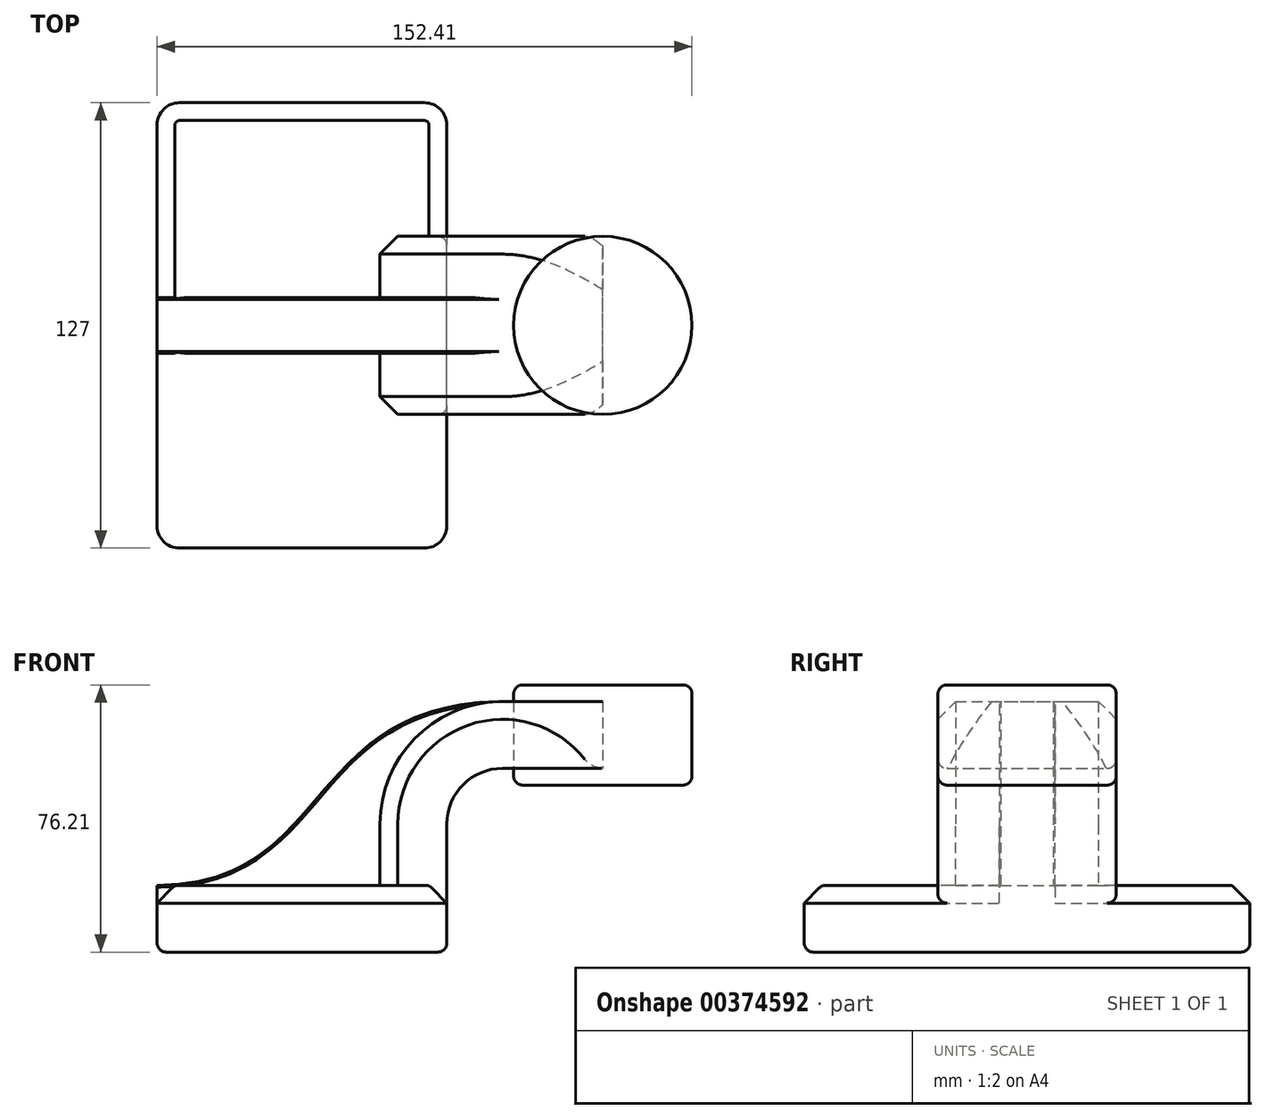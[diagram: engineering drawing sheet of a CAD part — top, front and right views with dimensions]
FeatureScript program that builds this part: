
annotation { "Feature Type Name" : "Feature", "Feature Type Description" : "" }
export const myFeature = defineFeature(function(context is Context, id is Id, definition is map)
    precondition{}
    {
        {
            var Q0;
            Q0=qCreatedBy(makeId("Front.planeOp"),FACE);
            var sketch = newSketch(context, id + "F0", { "sketchPlane" : qUnion([Q0])});
            skLineSegment(sketch, "E0.bottom", {"start": v(-41.28, 9.52) * mm, "end": v(41.27, 9.53) * mm});
            skLineSegment(sketch, "E0.top", {"start": v(-41.28, -9.53) * mm, "end": v(41.28, -9.53) * mm});
            skLineSegment(sketch, "E0.left", {"start": v(-41.28, 9.52) * mm, "end": v(-41.27, -9.53) * mm});
            skLineSegment(sketch, "E0.right", {"start": v(41.28, 9.53) * mm, "end": v(41.28, -9.52) * mm});
            skPoint(sketch, "E0.middle", {"position": v(0, 0) * mm});
            skLineSegment(sketch, "E1.bottom", {"start": v(60.32, 66.68) * mm, "end": v(111.12, 66.68) * mm});
            skLineSegment(sketch, "E1.top", {"start": v(60.32, 38.1) * mm, "end": v(111.12, 38.1) * mm});
            skLineSegment(sketch, "E1.left", {"start": v(60.32, 66.68) * mm, "end": v(60.32, 38.1) * mm});
            skLineSegment(sketch, "E1.right", {"start": v(111.12, 66.68) * mm, "end": v(111.12, 38.1) * mm});
            skPoint(sketch, "E1.middle", {"position": v(85.72, 52.39) * mm});
            skLineSegment(sketch, "E2", {"start": v(41.27, 9.53) * mm, "end": v(41.27, 27) * mm});
            skArc(sketch, "E3", {"start": v(41.27, 27) * mm, "mid": v(45.92, 38.23) * mm, "end": v(57.15, 42.88) * mm});
            skLineSegment(sketch, "E4", {"start": v(57.15, 42.88) * mm, "end": v(85.72, 42.88) * mm});
            skPoint(sketch, "E4.endSnap0", {"position": v(85.72, 38.1) * mm});
            skLineSegment(sketch, "E5.0", {"start": v(57.15, 61.93) * mm, "end": v(85.72, 61.93) * mm});
            skArc(sketch, "E5.1", {"start": v(22.22, 27) * mm, "mid": v(32.45, 51.7) * mm, "end": v(57.15, 61.93) * mm});
            skLineSegment(sketch, "E5.2", {"start": v(22.22, 9.53) * mm, "end": v(22.22, 27) * mm});
            skLineSegment(sketch, "E6", {"start": v(85.72, 38.1) * mm, "end": v(85.72, 66.68) * mm});
            skFitSpline(sketch, "E7", {"points": [v(-41.28, 9.52) * mm, v(57.15, 61.93) * mm], "startDerivative": vector(150.82, 0) * mm, "endDerivative": vector(171.45, 1.6) * mm});
            skSolve(sketch);
        }
        {
            var Q0;
            Q0=makeQuery(id+"F0.imprint","IMPRINT",FACE,{"disambiguationData":[TD([[makeQuery(id+"F0.imprint","IMPRINT",EDGE,{"derivedFrom":sQuery(id+"F0.wireOp",EDGE,"E0.top")}),1.0]])]});
            extrude(context, id + "F1", {"entities" : qUnion([Q0]), "endBound" : BoundingType.SYMMETRIC, "depth" : 127 * mm});
        }
        {
            var Q0;
            {var subQ1=sQuery(id+"F0.wireOp",EDGE,"E2");Q0=makeQuery(id+"F0.imprint","IMPRINT",FACE,{"disambiguationData":[TD([[makeQuery(id+"F0.imprint","IMPRINT",EDGE,{"derivedFrom":subQ1}),1.0]])]});}
            var Q1;
            {var subQ0=sQuery(id+"F0.wireOp",EDGE,"E5.0");var subQ1=sQuery(id+"F0.wireOp",EDGE,"E1.left");var subQ2=makeQuery(id+"F0.imprint","INTERSECT",VERTEX,{"derivedFrom":[subQ1,subQ0]});Q1=makeQuery(id+"F0.imprint","IMPRINT",FACE,{"disambiguationData":[TD([[makeQuery(id+"F0.imprint","IMPRINT",EDGE,{"disambiguationData":[TD([[subQ2,-1.0]])],"derivedFrom":subQ1}),1.0]])]});}
            extrude(context, id + "F2", {"entities" : qUnion([Q0, Q1]), "operationType" : NewBodyOperationType.ADD, "endBound" : BoundingType.SYMMETRIC, "depth" : 50.8 * mm});
        }
        {
            var Q0;
            {var subQ3=sQuery(id+"F0.wireOp",EDGE,"E5.2");Q0=makeQuery(id+"F0.imprint","IMPRINT",FACE,{"disambiguationData":[TD([[makeQuery(id+"F0.imprint","IMPRINT",EDGE,{"derivedFrom":subQ3}),1.0]])]});}
            extrude(context, id + "F3", {"entities" : qUnion([Q0]), "operationType" : NewBodyOperationType.ADD, "endBound" : BoundingType.SYMMETRIC, "depth" : 15.88 * mm});
        }
        {
            var Q0;
            {var subQ4=sQuery(id+"F0.wireOp",EDGE,"E1.right");Q0=makeQuery(id+"F0.imprint","IMPRINT",FACE,{"disambiguationData":[TD([[makeQuery(id+"F0.imprint","IMPRINT",EDGE,{"derivedFrom":subQ4}),-1.0]])]});}
            var Q1;
            Q1=sQuery(id+"F0.wireOp",EDGE,"E6");
            revolve(context, id + "F4", {"entities" : qUnion([Q0]), "axis" : qUnion([Q1]), "revolveType" : RevolveType.FULL});
        }
        {
            var Q0;
            Q0=makeQuery(id+"F1.opExtrude","CAP_EDGE",EDGE,{"disambiguationData":[OSD([sQuery(id+"F0.wireOp",EDGE,"E0.left")])],"isStart":false});
            var Q1;
            Q1=makeQuery(id+"F1.opExtrude","CAP_EDGE",EDGE,{"disambiguationData":[OSD([sQuery(id+"F0.wireOp",EDGE,"E0.right")])],"isStart":false});
            var Q2;
            Q2=makeQuery(id+"F1.opExtrude","CAP_EDGE",EDGE,{"disambiguationData":[OSD([sQuery(id+"F0.wireOp",EDGE,"E0.right")])],"isStart":true});
            var Q3;
            Q3=makeQuery(id+"F1.opExtrude","CAP_EDGE",EDGE,{"disambiguationData":[OSD([sQuery(id+"F0.wireOp",EDGE,"E0.left")])],"isStart":true});
            fillet(context, id + "F5", {"entities" : qUnion([Q0, Q1, Q2, Q3]), "radius" : 6.35 * mm, "tangentPropagation" : true, "allowEdgeOverflow" : false});
        }
        {
            var Q0;
            Q0=makeQuery(id+"F1.opExtrude","CAP_EDGE",EDGE,{"disambiguationData":[OSD([sQuery(id+"F0.wireOp",EDGE,"E0.bottom")])],"isStart":false});
            var Q1;
            {var subQ4=sQuery(id+"F0.wireOp",EDGE,"E0.bottom");var subQ5=sQuery(id+"F0.wireOp",EDGE,"E0.right");var subQ6=sQuery(id+"F0.wireOp",EDGE,"E0.left");Q1=makeQuery(id+"F5.opFillet","BLEND_EDGE",EDGE,{"blendedFrom":[makeQuery(id+"F1.opExtrude","CAP_EDGE",EDGE,{"disambiguationData":[OSD([subQ6])],"isStart":false}),makeQuery(id+"F3.boolean.opBoolean","SPLIT",FACE,{"disambiguationData":[TD([makeQuery(id+"F1.opExtrude","CAP_FACE",FACE,{"disambiguationData":[OSD([subQ4,sQuery(id+"F0.wireOp",EDGE,"E0.top"),subQ6,subQ5])],"isStart":false})])],"derivedFrom":makeQuery(id+"F1.opExtrude","SWEPT_FACE",FACE,{"disambiguationData":[OSD([subQ4])]})})],"blendedInto":[makeQuery(id+"F3.boolean.opBoolean","SPLIT",FACE,{"disambiguationData":[TD([makeQuery(id+"F1.opExtrude","CAP_FACE",FACE,{"disambiguationData":[OSD([subQ4,sQuery(id+"F0.wireOp",EDGE,"E0.top"),subQ6,subQ5])],"isStart":false})])],"derivedFrom":makeQuery(id+"F1.opExtrude","SWEPT_FACE",FACE,{"disambiguationData":[OSD([subQ4])]})})]});}
            var Q2;
            {var subQ4=sQuery(id+"F0.wireOp",EDGE,"E0.bottom");var subQ5=sQuery(id+"F0.wireOp",EDGE,"E0.right");var subQ6=sQuery(id+"F0.wireOp",EDGE,"E0.left");Q2=makeQuery(id+"F5.opFillet","BLEND_EDGE",EDGE,{"blendedFrom":[makeQuery(id+"F1.opExtrude","CAP_EDGE",EDGE,{"disambiguationData":[OSD([subQ5])],"isStart":false}),makeQuery(id+"F3.boolean.opBoolean","SPLIT",FACE,{"disambiguationData":[TD([makeQuery(id+"F1.opExtrude","CAP_FACE",FACE,{"disambiguationData":[OSD([subQ4,sQuery(id+"F0.wireOp",EDGE,"E0.top"),subQ6,subQ5])],"isStart":false})])],"derivedFrom":makeQuery(id+"F1.opExtrude","SWEPT_FACE",FACE,{"disambiguationData":[OSD([subQ4])]})})],"blendedInto":[makeQuery(id+"F3.boolean.opBoolean","SPLIT",FACE,{"disambiguationData":[TD([makeQuery(id+"F1.opExtrude","CAP_FACE",FACE,{"disambiguationData":[OSD([subQ4,sQuery(id+"F0.wireOp",EDGE,"E0.top"),subQ6,subQ5])],"isStart":false})])],"derivedFrom":makeQuery(id+"F1.opExtrude","SWEPT_FACE",FACE,{"disambiguationData":[OSD([subQ4])]})})]});}
            var Q3;
            {var subQ0=sQuery(id+"F0.wireOp",EDGE,"E2");var subQ1=sQuery(id+"F0.wireOp",EDGE,"E0.bottom");var subQ2=sQuery(id+"F0.wireOp",EDGE,"E0.right");Q3=makeQuery(id+"F2.boolean.opBoolean","SPLIT",EDGE,{"disambiguationData":[TD([makeQuery(id+"F1.opExtrude","CAP_FACE",FACE,{"disambiguationData":[OSD([subQ1,sQuery(id+"F0.wireOp",EDGE,"E0.top"),sQuery(id+"F0.wireOp",EDGE,"E0.left"),subQ2])],"isStart":false})])],"derivedFrom":makeQuery(id+"F1.opExtrude","SWEPT_EDGE",EDGE,{"disambiguationData":[OSD([subQ1,subQ2,subQ0])]})});}
            var Q4;
            {var subQ0=sQuery(id+"F0.wireOp",EDGE,"E7");var subQ1=sQuery(id+"F0.wireOp",EDGE,"E0.bottom");var subQ2=sQuery(id+"F0.wireOp",EDGE,"E0.left");Q4=makeQuery(id+"F3.boolean.opBoolean","SPLIT",EDGE,{"disambiguationData":[TD([makeQuery(id+"F1.opExtrude","CAP_FACE",FACE,{"disambiguationData":[OSD([subQ1,sQuery(id+"F0.wireOp",EDGE,"E0.top"),subQ2,sQuery(id+"F0.wireOp",EDGE,"E0.right")])],"isStart":false})])],"derivedFrom":makeQuery(id+"F1.opExtrude","SWEPT_EDGE",EDGE,{"disambiguationData":[OSD([subQ1,subQ2,subQ0])]})});}
            var Q5;
            {var subQ0=sQuery(id+"F0.wireOp",EDGE,"E0.left");var subQ1=sQuery(id+"F0.wireOp",EDGE,"E7");var subQ2=sQuery(id+"F0.wireOp",EDGE,"E0.bottom");Q5=makeQuery(id+"F3.boolean.opBoolean","SPLIT",EDGE,{"disambiguationData":[TD([makeQuery(id+"F1.opExtrude","CAP_FACE",FACE,{"disambiguationData":[OSD([subQ2,sQuery(id+"F0.wireOp",EDGE,"E0.top"),subQ0,sQuery(id+"F0.wireOp",EDGE,"E0.right")])],"isStart":true})])],"derivedFrom":makeQuery(id+"F1.opExtrude","SWEPT_EDGE",EDGE,{"disambiguationData":[OSD([subQ2,subQ0,subQ1])]})});}
            var Q6;
            {var subQ4=sQuery(id+"F0.wireOp",EDGE,"E0.bottom");var subQ5=sQuery(id+"F0.wireOp",EDGE,"E0.right");var subQ6=sQuery(id+"F0.wireOp",EDGE,"E0.left");Q6=makeQuery(id+"F5.opFillet","BLEND_EDGE",EDGE,{"blendedFrom":[makeQuery(id+"F1.opExtrude","CAP_EDGE",EDGE,{"disambiguationData":[OSD([subQ6])],"isStart":true}),makeQuery(id+"F3.boolean.opBoolean","SPLIT",FACE,{"disambiguationData":[TD([makeQuery(id+"F1.opExtrude","CAP_FACE",FACE,{"disambiguationData":[OSD([subQ4,sQuery(id+"F0.wireOp",EDGE,"E0.top"),subQ6,subQ5])],"isStart":true})])],"derivedFrom":makeQuery(id+"F1.opExtrude","SWEPT_FACE",FACE,{"disambiguationData":[OSD([subQ4])]})})],"blendedInto":[makeQuery(id+"F3.boolean.opBoolean","SPLIT",FACE,{"disambiguationData":[TD([makeQuery(id+"F1.opExtrude","CAP_FACE",FACE,{"disambiguationData":[OSD([subQ4,sQuery(id+"F0.wireOp",EDGE,"E0.top"),subQ6,subQ5])],"isStart":true})])],"derivedFrom":makeQuery(id+"F1.opExtrude","SWEPT_FACE",FACE,{"disambiguationData":[OSD([subQ4])]})})]});}
            var Q7;
            Q7=makeQuery(id+"F1.opExtrude","CAP_EDGE",EDGE,{"disambiguationData":[OSD([sQuery(id+"F0.wireOp",EDGE,"E0.bottom")])],"isStart":true});
            var Q8;
            {var subQ4=sQuery(id+"F0.wireOp",EDGE,"E0.bottom");var subQ5=sQuery(id+"F0.wireOp",EDGE,"E0.right");var subQ6=sQuery(id+"F0.wireOp",EDGE,"E0.left");Q8=makeQuery(id+"F5.opFillet","BLEND_EDGE",EDGE,{"blendedFrom":[makeQuery(id+"F1.opExtrude","CAP_EDGE",EDGE,{"disambiguationData":[OSD([subQ5])],"isStart":true}),makeQuery(id+"F3.boolean.opBoolean","SPLIT",FACE,{"disambiguationData":[TD([makeQuery(id+"F1.opExtrude","CAP_FACE",FACE,{"disambiguationData":[OSD([subQ4,sQuery(id+"F0.wireOp",EDGE,"E0.top"),subQ6,subQ5])],"isStart":true})])],"derivedFrom":makeQuery(id+"F1.opExtrude","SWEPT_FACE",FACE,{"disambiguationData":[OSD([subQ4])]})})],"blendedInto":[makeQuery(id+"F3.boolean.opBoolean","SPLIT",FACE,{"disambiguationData":[TD([makeQuery(id+"F1.opExtrude","CAP_FACE",FACE,{"disambiguationData":[OSD([subQ4,sQuery(id+"F0.wireOp",EDGE,"E0.top"),subQ6,subQ5])],"isStart":true})])],"derivedFrom":makeQuery(id+"F1.opExtrude","SWEPT_FACE",FACE,{"disambiguationData":[OSD([subQ4])]})})]});}
            var Q9;
            {var subQ0=sQuery(id+"F0.wireOp",EDGE,"E2");var subQ1=sQuery(id+"F0.wireOp",EDGE,"E0.bottom");var subQ2=sQuery(id+"F0.wireOp",EDGE,"E0.right");Q9=makeQuery(id+"F2.boolean.opBoolean","SPLIT",EDGE,{"disambiguationData":[TD([makeQuery(id+"F1.opExtrude","CAP_FACE",FACE,{"disambiguationData":[OSD([subQ1,sQuery(id+"F0.wireOp",EDGE,"E0.top"),sQuery(id+"F0.wireOp",EDGE,"E0.left"),subQ2])],"isStart":true})])],"derivedFrom":makeQuery(id+"F1.opExtrude","SWEPT_EDGE",EDGE,{"disambiguationData":[OSD([subQ1,subQ2,subQ0])]})});}
            var Q10;
            Q10=makeQuery(id+"F2.opExtrude","CAP_EDGE",EDGE,{"disambiguationData":[OSD([sQuery(id+"F0.wireOp",EDGE,"E5.2")])],"isStart":false});
            var Q11;
            Q11=makeQuery(id+"F2.opExtrude","CAP_EDGE",EDGE,{"disambiguationData":[OSD([sQuery(id+"F0.wireOp",EDGE,"E5.1")])],"isStart":true});
            chamfer(context, id + "F6", {"entities" : qUnion([Q0, Q1, Q2, Q3, Q4, Q5, Q6, Q7, Q8, Q9, Q10, Q11]), "width" : 5.08 * mm, "tangentPropagation" : true});
        }
        {
            var Q0;
            Q0=makeQuery(id+"F3.opExtrude","CAP_EDGE",EDGE,{"disambiguationData":[OSD([sQuery(id+"F0.wireOp",EDGE,"E7")])],"isStart":false});
            var Q1;
            Q1=makeQuery(id+"F3.opExtrude","CAP_EDGE",EDGE,{"disambiguationData":[OSD([sQuery(id+"F0.wireOp",EDGE,"E7")])],"isStart":true});
            chamfer(context, id + "F7", {"entities" : qUnion([Q0, Q1]), "width" : 0.5 * mm, "tangentPropagation" : true});
        }
        {
            var Q0;
            Q0=makeQuery(id+"F4.opRevolve","SWEPT_EDGE",EDGE,{"disambiguationData":[OSD([sQuery(id+"F0.wireOp",EDGE,"E1.bottom"),sQuery(id+"F0.wireOp",EDGE,"E1.right")])]});
            var Q1;
            Q1=makeQuery(id+"F4.opRevolve","SWEPT_EDGE",EDGE,{"disambiguationData":[OSD([sQuery(id+"F0.wireOp",EDGE,"E1.top"),sQuery(id+"F0.wireOp",EDGE,"E1.right")])]});
            var Q2;
            Q2=makeQuery(id+"F1.opExtrude","SWEPT_EDGE",EDGE,{"disambiguationData":[OSD([sQuery(id+"F0.wireOp",EDGE,"E0.top"),sQuery(id+"F0.wireOp",EDGE,"E0.left")])]});
            var Q3;
            Q3=makeQuery(id+"F2.opExtrude","CAP_EDGE",EDGE,{"disambiguationData":[OSD([sQuery(id+"F0.wireOp",EDGE,"E3")])],"isStart":true});
            var Q4;
            Q4=makeQuery(id+"F2.opExtrude","CAP_EDGE",EDGE,{"disambiguationData":[OSD([sQuery(id+"F0.wireOp",EDGE,"E3")])],"isStart":false});
            var Q5;
            {var subQ4=sQuery(id+"F0.wireOp",EDGE,"E0.bottom");var subQ5=sQuery(id+"F0.wireOp",EDGE,"E0.right");var subQ6=sQuery(id+"F0.wireOp",EDGE,"E0.left");Q5=makeQuery(id+"F6.opChamfer","BLEND_EDGE",EDGE,{"blendedFrom":[makeQuery(id+"F1.opExtrude","CAP_EDGE",EDGE,{"disambiguationData":[OSD([subQ4])],"isStart":false}),makeQuery(id+"F3.boolean.opBoolean","SPLIT",FACE,{"disambiguationData":[TD([makeQuery(id+"F1.opExtrude","CAP_FACE",FACE,{"disambiguationData":[OSD([subQ4,sQuery(id+"F0.wireOp",EDGE,"E0.top"),subQ6,subQ5])],"isStart":false})])],"derivedFrom":makeQuery(id+"F1.opExtrude","SWEPT_FACE",FACE,{"disambiguationData":[OSD([subQ4])]})})],"blendedInto":[makeQuery(id+"F3.boolean.opBoolean","SPLIT",FACE,{"disambiguationData":[TD([makeQuery(id+"F1.opExtrude","CAP_FACE",FACE,{"disambiguationData":[OSD([subQ4,sQuery(id+"F0.wireOp",EDGE,"E0.top"),subQ6,subQ5])],"isStart":false})])],"derivedFrom":makeQuery(id+"F1.opExtrude","SWEPT_FACE",FACE,{"disambiguationData":[OSD([subQ4])]})})]});}
            fillet(context, id + "F8", {"entities" : qUnion([Q0, Q1, Q2, Q3, Q4, Q5]), "radius" : 2.54 * mm, "tangentPropagation" : true, "allowEdgeOverflow" : false});
        }
    });
